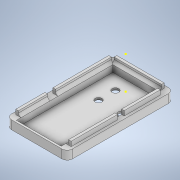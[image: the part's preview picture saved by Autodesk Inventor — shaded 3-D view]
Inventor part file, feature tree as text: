
AUTODESK INVENTOR PART (.ipt)
format: ipt  version: 2022 (Build 260153000, 153)  size: 927,232 bytes
history: native  units: mm
features: sketch x21, extrude x20, fillet x7, other x3, plane x2, chamfer x1, move_body x1, shell x1
ambient origin geometry x8: Origin, YZ Plane, XZ Plane, XY Plane, X Axis, Y Axis, Z Axis, Center Point
bodies: Body1 (feature_tree), Body2 (feature_tree), Body3 (feature_tree), Body4 (feature_tree)
feature tree (56):
  other  "Control"
  extrude  "Extrusion1"  Depth=28.8mm
  extrude  "Extrusion2"  Depth=14.7mm
  extrude  "Extrusion3"  Depth=2.36mm
  extrude  "Extrusion4"  Depth=7.9mm
  extrude  "Extrusion6"  Depth=8.55mm
  extrude  "Extrusion7"  Depth=2.36mm
  chamfer  "Chamfer1"  Distance=8.5mm
  extrude  "Extrusion8"  Depth=10.17mm
  extrude  "Extrusion9"  Depth=11.0mm
  plane  "Work Plane2"
  extrude  "Extrusion10"  Depth=9.44mm
  extrude  "Extrusion11"  Depth=4.82mm
  extrude  "Extrusion12"  Depth=10.0mm
  move_body  "Move Body1"
  plane  "Work Plane4"
  extrude  "Extrusion13"  Depth=0.4mm
  extrude  "Extrusion14"  Depth=11.13mm
  extrude  "Extrusion15"  Depth=0.61mm
  sketch  "Sketch16"  dims[d40=12.7mm d41=11.13mm]
  extrude  "Extrusion16"  Depth=0.61mm
  extrude  "Extrusion17"  Depth=0.61mm
  fillet  "Fillet1"  Radius=0.61mm
  fillet  "Fillet2"  Radius=1.0mm
  fillet  "Fillet3"  Radius=1.0mm
  extrude  "Extrusion18"  Depth=2.085mm
  extrude  "Extrusion19"  Depth=0.925mm
  extrude  "Extrusion20"  Depth=5.8mm TaperAngle=0.0deg
  fillet  "Fillet4"  Radius=0.4mm
  fillet  "Fillet5"  Radius=0.2mm
  fillet  "Fillet6"  Radius=0.2mm
  fillet  "Fillet7"  Radius=0.2mm
  sketch  "Sketch23"  dims[d56=0.925mm d57=5.8mm d58=0.0mm]
  extrude  "Extrusion21"  Depth=2.0mm
  sketch  "Sketch1"  dims[d0=29.4mm d1=28.8mm]
  sketch  "Sketch2"  dims[d2=14.4mm d3=14.7mm]
  sketch  "Sketch3"  dims[d4=1.57mm d5=0.0mm d6=2.36mm]
  sketch  "Sketch4"  dims[d7=11.49mm d8=7.9mm]
  sketch  "Sketch6"  dims[d9=0.77mm d10=8.55mm]
  sketch  "Sketch7"  dims[d11=0.6mm d12=2.36mm]
  sketch  "Sketch8"  dims[d13=0.4mm d14=8.5mm d15=0.0mm]
  other  "Buttons"
  sketch  "Sketch9"  dims[d16=10.15mm d17=10.17mm]
  sketch  "Sketch11"  dims[d18=5.0mm d19=11.0mm]
  sketch  "Sketch12"  dims[d20=8.0mm d21=0.0mm d22=9.44mm]
  sketch  "Sketch13"  dims[d23=4.82mm d24=4.82mm]
  sketch  "Sketch14"  dims[d25=7.0mm d26=10.0mm d27=0.0mm d28=0.0mm d37=4.97mm]
  sketch  "Sketch15"  dims[d38=8.0mm d39=0.4mm]
  sketch  "Sketch17"  dims[d42=2.55mm d43=0.0mm d44=0.61mm]
  sketch  "Sketch18"  dims[d45=0.61mm d46=0.61mm]
  sketch  "Sketch19"  dims[d47=0.61mm d48=0.61mm d49=0.61mm d50=1.0mm d51=1.0mm]
  other  "Lid"
  shell  "Shell"  Thickness=2.2mm
  sketch  "Sketch20"  dims[d52=2.085mm d53=2.085mm]
  sketch  "Sketch21"  dims[d54=1.9mm d55=0.925mm]
  sketch  "Sketch24"  dims[d59=0.2mm d60=2.0mm d61=45.0deg d62=0.4mm d63=0.2mm d64=0.2mm d65=1.9425mm d66=0.4mm d67=0.4mm d68=0.4mm d69=1.9425mm d70=2.0mm d71=2.0mm d72=2.005mm d73=0.2mm d74=0.2mm d75=0.2mm d76=0.2mm d77=0.2mm d83=2.2mm d84=0.2mm d85=2.2mm d86=2.345mm d90=0.4mm d91=0.4mm d92=0.2mm d93=2.54mm d94=0.0mm d102=0.61mm d103=0.61mm d112=0.2mm d113=0.2mm d114=0.4mm d115=0.2mm d117=2.345mm d118=1.075mm d119=0.875mm d120=0.875mm d121=2.3mm d122=0.61mm d123=0.61mm d124=0.61mm d125=2.3mm d126=2.3mm d127=1.075mm d128=2.65mm d129=0.0mm d130=28.7mm d131=32.7mm d134=1.6mm d135=0.0mm d136=6.0mm d137=6.0mm d138=6.0mm d139=6.0mm d140=2.3mm d141=11.53mm d142=2.6mm d143=6.7mm d144=4.0mm d145=0.0mm d146=3.5mm d147=3.5mm d148=3.5mm d149=3.5mm d150=3.0mm d151=3.0mm d152=3.0mm d153=3.0mm d154=4.55mm d155=-0.349066mm d158=180.0deg d159=5.0mm d160=-14.0mm d161=-8.0mm d162=2.0mm d163=45.0mm d164=3.0mm d165=13.0mm d166=2.5mm d167=7.0mm d168=10.0mm d173=1.5mm d174=0.0mm d175=2.0mm d176=2.0mm d177=2.0mm d178=2.0mm d179=30.0mm d180=0.0mm d181=1.0mm d182=2.0mm d183=22.0mm d184=0.0mm d185=45.813165mm d187=24.5mm d188=2.313165mm d189=4.0mm d190=1.0mm d191=2.0mm d192=2.0mm d193=2.0mm d194=1.0mm d195=2.0mm d197=15.0mm d199=25.0mm d200=11.3mm d201=23.0mm d202=22.813165mm d203=22.0mm d204=-2.094395mm d205=4.0mm d206=5.0mm d207=4.0mm d208=22.0mm d209=0.0mm d210=4.0mm d211=3.0mm d212=1.0mm d213=4.0mm d214=5.0mm d215=5.0mm d216=5.0mm d217=5.0mm d218=6.5mm d219=0.0mm d220=25.0mm d221=11.3mm d222=32.2mm d224=2.0mm d225=2.0mm d231=1.015mm d232=1.015mm d233=1.0mm d234=1.0mm d237=35.0mm d238=2.0mm d239=22.0mm d240=6.0mm d241=2.0mm d242=3.5mm d243=0.0mm d244=10.0mm d245=8.0mm d246=3.0mm d247=2.0mm d248=4.0mm d249=0.0mm d250=8.0mm d251=2.0mm d252=5.0mm d253=11.0mm d254=3.0mm d255=2.0mm d256=10.25mm d257=0.0mm d258=1.0mm d259=1.0mm d260=1.0mm d261=2.0mm d262=2.0mm d263=5.0mm d264=4.0mm d265=5.0mm d266=5.0mm d267=0.0mm d268=1.5mm]
